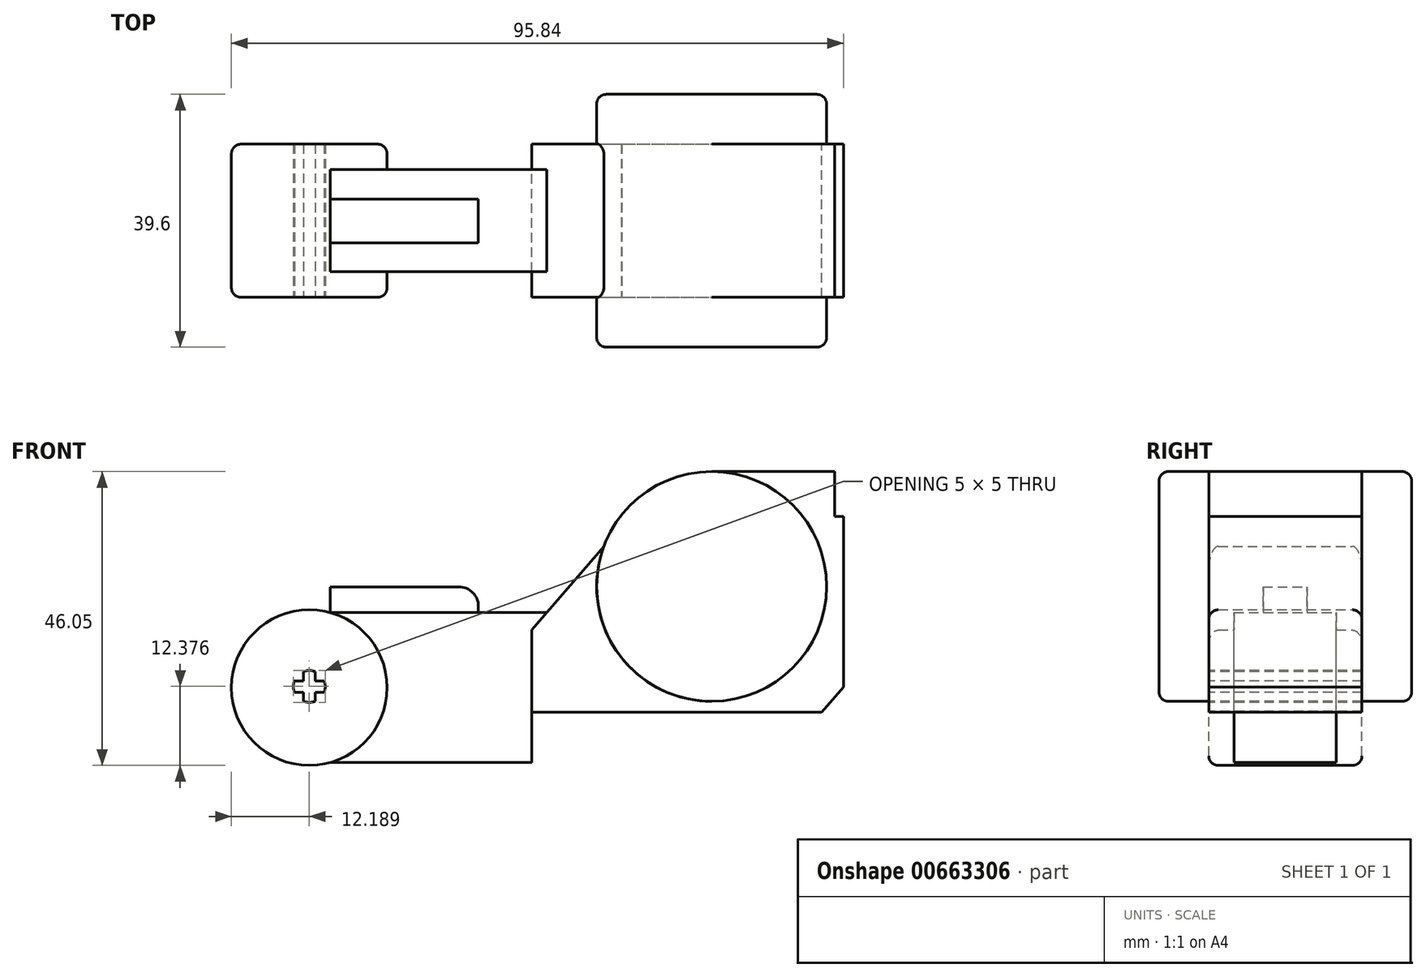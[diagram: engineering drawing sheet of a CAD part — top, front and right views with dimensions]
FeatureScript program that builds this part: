
annotation { "Feature Type Name" : "Feature", "Feature Type Description" : "" }
export const myFeature = defineFeature(function(context is Context, id is Id, definition is map)
    precondition{}
    {
        {
            var Q0;
            Q0=qCreatedBy(makeId("Front.planeOp"),FACE);
            var sketch = newSketch(context, id + "F0", { "sketchPlane" : qUnion([Q0])});
            skLineSegment(sketch, "E0.bottom", {"start": v(16.93, 23.2) * mm, "end": v(-2.37, 23.2) * mm});
            skLineSegment(sketch, "E0.top", {"start": v(7.98, -22.4) * mm, "end": v(-62.12, -22.4) * mm});
            skLineSegment(sketch, "E0.left", {"start": v(30.68, 16.16) * mm, "end": v(30.68, -6.44) * mm});
            skPoint(sketch, "E0.middle", {"position": v(-23.2, 0.4) * mm});
            skLineSegment(sketch, "E1.bottom", {"start": v(-62.12, -22.4) * mm, "end": v(7.98, -22.4) * mm});
            skLineSegment(sketch, "E2.bottom", {"start": v(-62.12, -22.4) * mm, "end": v(-30.52, -22.4) * mm});
            skPoint(sketch, "E3.endSnap0", {"position": v(30.68, 0.4) * mm});
            skLineSegment(sketch, "E4.right", {"start": v(30.68, -14.8) * mm, "end": v(30.68, -14.5) * mm});
            skPoint(sketch, "E5.oppositeSnap0", {"position": v(24.48, 14.62) * mm});
            skLineSegment(sketch, "E5.bottom", {"start": v(7.98, -22.4) * mm, "end": v(-30.52, -22.4) * mm});
            skLineSegment(sketch, "E6.bottom", {"start": v(-30.52, -22.4) * mm, "end": v(7.98, -22.4) * mm});
            skLineSegment(sketch, "E6.top", {"start": v(-30.52, -4.4) * mm, "end": v(-17.6, -4.4) * mm});
            skLineSegment(sketch, "E6.left", {"start": v(-30.52, -22.4) * mm, "end": v(-30.52, -4.4) * mm});
            skLineSegment(sketch, "E7.bottom", {"start": v(-2.37, 23.2) * mm, "end": v(16.93, 23.2) * mm});
            skLineSegment(sketch, "E7.top", {"start": v(-31.78, -14.5) * mm, "end": v(14.85, -14.5) * mm});
            skLineSegment(sketch, "E8", {"start": v(68.58, 23.2) * mm, "end": v(68.58, 5.2) * mm, "construction": true});
            skPoint(sketch, "E9.endSnap0", {"position": v(68.58, 5.2) * mm});
            skLineSegment(sketch, "E10", {"start": v(-2.37, 5.2) * mm, "end": v(-2.37, 31.5) * mm, "construction": true});
            skPoint(sketch, "E10.startSnap0", {"position": v(-2.37, 31.5) * mm});
            skCircle(sketch, "E11", {"center": v(-2.37, 5.2) * mm, "radius": 18 * mm});
            skPoint(sketch, "E12.end.orphan", {"position": v(15.63, 38.6) * mm});
            skPoint(sketch, "E12.start.orphan", {"position": v(-77.07, 38.6) * mm});
            skPoint(sketch, "E13.orphan", {"position": v(68.58, -12.8) * mm});
            skLineSegment(sketch, "E14.trimOffspring", {"start": v(18.28, 5.2) * mm, "end": v(-2.37, 5.2) * mm, "construction": true});
            skPoint(sketch, "E9.start.orphan", {"position": v(68.58, 5.2) * mm});
            skLineSegment(sketch, "E15.bottom", {"start": v(-62.12, -22.4) * mm, "end": v(-14.02, -22.4) * mm});
            skLineSegment(sketch, "E15.top", {"start": v(-62.12, 1.1) * mm, "end": v(-28.16, 1.1) * mm});
            skLineSegment(sketch, "E16", {"start": v(30.68, 0.4) * mm, "end": v(18.28, 0.55) * mm, "construction": true});
            skLineSegment(sketch, "E17", {"start": v(-28.16, 1.1) * mm, "end": v(-19.23, 11.5) * mm});
            skPoint(sketch, "E18.orphan", {"position": v(-77.07, 23.2) * mm});
            skPoint(sketch, "E19.orphan", {"position": v(-30.52, 23.2) * mm});
            skLineSegment(sketch, "E20", {"start": v(41.56, -22.4) * mm, "end": v(41.56, 16.16) * mm, "construction": true});
            skLineSegment(sketch, "E21", {"start": v(18.28, 16.16) * mm, "end": v(30.68, 16.16) * mm});
            skLineSegment(sketch, "E22", {"start": v(18.28, 16.16) * mm, "end": v(18.28, -6.3) * mm});
            skLineSegment(sketch, "E23", {"start": v(18.28, -6.3) * mm, "end": v(30.68, -6.44) * mm});
            skLineSegment(sketch, "E24", {"start": v(18.28, -6.3) * mm, "end": v(18.28, -10.54) * mm});
            skPoint(sketch, "E3.end.orphan", {"position": v(30.68, -14.8) * mm});
            skLineSegment(sketch, "E25", {"start": v(18.28, -10.54) * mm, "end": v(7.98, -22.4) * mm});
            skLineSegment(sketch, "E26", {"start": v(-77.07, 13.22) * mm, "end": v(-53.67, 13.22) * mm, "construction": true});
            skCircle(sketch, "E27", {"center": v(-65.37, -10.64) * mm, "radius": 12.2 * mm});
            skPoint(sketch, "E27.centerSnap0", {"position": v(-65.37, 13.22) * mm});
            skPoint(sketch, "E27.centerSnap1", {"position": v(-77.07, -10.64) * mm});
            skPoint(sketch, "E0.right.start.orphan", {"position": v(-77.07, 1.1) * mm});
            skPoint(sketch, "E28.orphan", {"position": v(-77.07, -22.4) * mm});
            skLineSegment(sketch, "E29", {"start": v(-28.16, 1.1) * mm, "end": v(-30.52, -1.63) * mm});
            skLineSegment(sketch, "E30", {"start": v(-30.52, -1.63) * mm, "end": v(-30.52, -4.4) * mm});
            skLineSegment(sketch, "E31.top", {"start": v(30.68, 16.16) * mm, "end": v(16.93, 16.16) * mm});
            skLineSegment(sketch, "E31.right", {"start": v(16.93, 23.2) * mm, "end": v(16.93, 16.16) * mm});
            skPoint(sketch, "E32.orphan", {"position": v(30.68, 23.2) * mm});
            skLineSegment(sketch, "E33.trimOffspring", {"start": v(30.68, -6.44) * mm, "end": v(30.68, -4.4) * mm});
            skLineSegment(sketch, "E34.trimOffspring", {"start": v(30.68, -6.44) * mm, "end": v(30.68, 14.62) * mm});
            skLineSegment(sketch, "E35.trimOffspring", {"start": v(30.68, -14.5) * mm, "end": v(30.68, -14.8) * mm});
            skPoint(sketch, "E36.orphan", {"position": v(30.68, -22.4) * mm});
            skLineSegment(sketch, "E37", {"start": v(18.28, -10.54) * mm, "end": v(18.28, -14.5) * mm});
            skPoint(sketch, "E38.trimOffspring.end.orphan", {"position": v(18.28, -14.8) * mm});
            skLineSegment(sketch, "E39", {"start": v(18.28, -14.5) * mm, "end": v(14.85, -14.5) * mm});
            skLineSegment(sketch, "E40", {"start": v(-30.52, -22.4) * mm, "end": v(-30.52, -14.5) * mm});
            skLineSegment(sketch, "E41", {"start": v(-30.52, -14.5) * mm, "end": v(-16.42, -14.5) * mm});
            skLineSegment(sketch, "E42", {"start": v(-30.52, -22.4) * mm, "end": v(-23.37, -22.4) * mm});
            skSolve(sketch);
        }
        {
            var Q0;
            {var subQ0=sQuery(id+"F0.wireOp",EDGE,"E11");var subQ1=makeQuery(id+"F0.imprint","INTERSECT",VERTEX,{"derivedFrom":[sQuery(id+"F0.wireOp",EDGE,"E7.bottom"),subQ0]});Q0=makeQuery(id+"F0.imprint","IMPRINT",FACE,{"disambiguationData":[TD([[makeQuery(id+"F0.imprint","IMPRINT",EDGE,{"disambiguationData":[TD([[subQ1,-1.0]])],"derivedFrom":subQ0}),1.0]])]});}
            extrude(context, id + "F1", {"entities" : qUnion([Q0]), "endBound" : BoundingType.SYMMETRIC, "oppositeDirection" : true, "depth" : 39.6 * mm, "offsetDistance" : 25 * mm});
        }
        {
            var Q0;
            {var subQ1=sQuery(id+"F0.wireOp",EDGE,"E6.bottom");Q0=makeQuery(id+"F0.imprint","IMPRINT",FACE,{"disambiguationData":[TD([[makeQuery(id+"F0.imprint","IMPRINT",EDGE,{"derivedFrom":subQ1}),1.0]])]});}
            var Q1;
            {var subQ4=sQuery(id+"F0.wireOp",EDGE,"E6.top");Q1=makeQuery(id+"F0.imprint","IMPRINT",FACE,{"disambiguationData":[TD([[makeQuery(id+"F0.imprint","IMPRINT",EDGE,{"derivedFrom":subQ4}),-1.0]])]});}
            var Q2;
            {var subQ2=sQuery(id+"F0.wireOp",EDGE,"E6.top");Q2=makeQuery(id+"F0.imprint","IMPRINT",FACE,{"disambiguationData":[TD([[makeQuery(id+"F0.imprint","IMPRINT",EDGE,{"derivedFrom":subQ2}),1.0]])]});}
            var Q3;
            {var subQ1=sQuery(id+"F0.wireOp",EDGE,"E0.left");Q3=makeQuery(id+"F0.imprint","IMPRINT",FACE,{"disambiguationData":[TD([[makeQuery(id+"F0.imprint","IMPRINT",EDGE,{"derivedFrom":subQ1}),-1.0]])]});}
            extrude(context, id + "F2", {"entities" : qUnion([Q0, Q1, Q2, Q3]), "operationType" : NewBodyOperationType.ADD, "endBound" : BoundingType.SYMMETRIC, "depth" : 24 * mm, "offsetDistance" : 25 * mm});
        }
        {
            var Q0;
            {var subQ7=sQuery(id+"F0.wireOp",EDGE,"E15.top");Q0=makeQuery(id+"F0.imprint","IMPRINT",FACE,{"disambiguationData":[TD([[makeQuery(id+"F0.imprint","IMPRINT",EDGE,{"derivedFrom":subQ7}),-1.0]])]});}
            extrude(context, id + "F3", {"entities" : qUnion([Q0]), "operationType" : NewBodyOperationType.ADD, "endBound" : BoundingType.SYMMETRIC, "depth" : 16 * mm, "offsetDistance" : 25 * mm});
        }
        {
            var Q0;
            {var subQ0=sQuery(id+"F0.wireOp",EDGE,"E27");var subQ1=makeQuery(id+"F0.imprint","INTERSECT",VERTEX,{"derivedFrom":[sQuery(id+"F0.wireOp",EDGE,"E15.bottom"),subQ0]});Q0=makeQuery(id+"F0.imprint","IMPRINT",FACE,{"disambiguationData":[TD([[makeQuery(id+"F0.imprint","IMPRINT",EDGE,{"disambiguationData":[TD([[subQ1,1.0]])],"derivedFrom":subQ0}),1.0]])]});}
            extrude(context, id + "F4", {"entities" : qUnion([Q0]), "operationType" : NewBodyOperationType.ADD, "endBound" : BoundingType.SYMMETRIC, "depth" : 24 * mm, "offsetDistance" : 25 * mm});
        }
        {
            var Q0;
            Q0=makeQuery(id+"F4.opExtrude","CAP_FACE",FACE,{"disambiguationData":[OSD([sQuery(id+"F0.wireOp",EDGE,"E27")])],"isStart":false});
            var sketch = newSketch(context, id + "F5", { "sketchPlane" : qUnion([Q0])});
            skCircle(sketch, "E43", {"center": v(-65.37, -10.46) * mm, "radius": 3.5 * mm});
            skCircle(sketch, "E44", {"center": v(-65.37, -10.46) * mm, "radius": 2.5 * mm});
            skLineSegment(sketch, "E45", {"start": v(-65.37, -10.46) * mm, "end": v(-66.27, -10.46) * mm});
            skLineSegment(sketch, "E46", {"start": v(-66.27, -10.46) * mm, "end": v(-64.47, -10.46) * mm});
            skLineSegment(sketch, "E47", {"start": v(-65.37, -10.46) * mm, "end": v(-65.37, -11.36) * mm});
            skLineSegment(sketch, "E48", {"start": v(-65.37, -11.36) * mm, "end": v(-65.37, -9.56) * mm});
            skLineSegment(sketch, "E49", {"start": v(-66.27, -9.6) * mm, "end": v(-67.72, -9.6) * mm});
            skLineSegment(sketch, "E50", {"start": v(-66.27, -9.6) * mm, "end": v(-66.27, -8.13) * mm});
            skLineSegment(sketch, "E51", {"start": v(-64.47, -9.6) * mm, "end": v(-64.47, -8.13) * mm});
            skLineSegment(sketch, "E52", {"start": v(-64.47, -9.6) * mm, "end": v(-63.02, -9.6) * mm});
            skLineSegment(sketch, "E53", {"start": v(-66.27, -11.36) * mm, "end": v(-67.7, -11.36) * mm});
            skLineSegment(sketch, "E54", {"start": v(-66.27, -11.36) * mm, "end": v(-66.27, -12.8) * mm});
            skLineSegment(sketch, "E55", {"start": v(-64.47, -11.36) * mm, "end": v(-64.47, -12.8) * mm});
            skLineSegment(sketch, "E56", {"start": v(-64.47, -11.36) * mm, "end": v(-63.04, -11.36) * mm});
            skSolve(sketch);
        }
        {
            var Q0;
            {var subQ4=sQuery(id+"F5.wireOp",EDGE,"E49");Q0=makeQuery(id+"F5.imprint","IMPRINT",FACE,{"disambiguationData":[TD([[makeQuery(id+"F5.imprint","IMPRINT",EDGE,{"derivedFrom":subQ4}),1.0]])]});}
            extrude(context, id + "F6", {"entities" : qUnion([Q0]), "operationType" : NewBodyOperationType.REMOVE, "oppositeDirection" : true, "depth" : 25 * mm, "offsetDistance" : 25 * mm});
        }
        {
            var Q0;
            Q0=makeQuery(id+"F4.opExtrude","CAP_EDGE",EDGE,{"disambiguationData":[OSD([sQuery(id+"F0.wireOp",EDGE,"E27")])],"isStart":true});
            fillet(context, id + "F7", {"entities" : qUnion([Q0]), "radius" : 1.5 * mm, "tangentPropagation" : true, "allowEdgeOverflow" : false});
        }
        {
            var Q0;
            Q0=makeQuery(id+"F4.opExtrude","CAP_EDGE",EDGE,{"disambiguationData":[OSD([sQuery(id+"F0.wireOp",EDGE,"E27")])],"isStart":false});
            fillet(context, id + "F8", {"entities" : qUnion([Q0]), "radius" : 1.5 * mm, "tangentPropagation" : true, "allowEdgeOverflow" : false});
        }
        {
            var Q0;
            Q0=makeQuery(id+"F2.opExtrude","CAP_EDGE",EDGE,{"disambiguationData":[OSD([sQuery(id+"F0.wireOp",EDGE,"E17"),sQuery(id+"F0.wireOp",EDGE,"E29")])],"isStart":false});
            fillet(context, id + "F9", {"entities" : qUnion([Q0]), "radius" : 1.5 * mm, "tangentPropagation" : true, "allowEdgeOverflow" : false});
        }
        {
            var Q0;
            Q0=makeQuery(id+"F2.opExtrude","CAP_EDGE",EDGE,{"disambiguationData":[OSD([sQuery(id+"F0.wireOp",EDGE,"E17"),sQuery(id+"F0.wireOp",EDGE,"E29")])],"isStart":true});
            fillet(context, id + "F10", {"entities" : qUnion([Q0]), "radius" : 1.5 * mm, "tangentPropagation" : true, "allowEdgeOverflow" : false});
        }
        {
            var Q0;
            Q0=makeQuery(id+"F1.opExtrude","CAP_EDGE",EDGE,{"disambiguationData":[OSD([sQuery(id+"F0.wireOp",EDGE,"E11")])],"isStart":false});
            fillet(context, id + "F11", {"entities" : qUnion([Q0]), "radius" : 1.5 * mm, "tangentPropagation" : true, "allowEdgeOverflow" : false});
        }
        {
            var Q0;
            Q0=makeQuery(id+"F1.opExtrude","CAP_EDGE",EDGE,{"disambiguationData":[OSD([sQuery(id+"F0.wireOp",EDGE,"E11")])],"isStart":true});
            fillet(context, id + "F12", {"entities" : qUnion([Q0]), "radius" : 1.5 * mm, "tangentPropagation" : true, "allowEdgeOverflow" : false});
        }
        {
            var Q0;
            Q0=makeQuery(id+"F2.opExtrude","CAP_FACE",FACE,{"disambiguationData":[OSD([sQuery(id+"F0.wireOp",EDGE,"E6.bottom"),sQuery(id+"F0.wireOp",EDGE,"E6.left"),sQuery(id+"F0.wireOp",EDGE,"E7.bottom"),sQuery(id+"F0.wireOp",EDGE,"E0.left"),sQuery(id+"F0.wireOp",EDGE,"E11"),sQuery(id+"F0.wireOp",EDGE,"E15.bottom"),sQuery(id+"F0.wireOp",EDGE,"E17"),sQuery(id+"F0.wireOp",EDGE,"E23"),sQuery(id+"F0.wireOp",EDGE,"E24"),sQuery(id+"F0.wireOp",EDGE,"E25"),sQuery(id+"F0.wireOp",EDGE,"E29"),sQuery(id+"F0.wireOp",EDGE,"E30"),sQuery(id+"F0.wireOp",EDGE,"E31.top"),sQuery(id+"F0.wireOp",EDGE,"E31.right"),sQuery(id+"F0.wireOp",EDGE,"E34.trimOffspring"),sQuery(id+"F0.wireOp",EDGE,"E40"),sQuery(id+"F0.wireOp",EDGE,"E42")])],"isStart":false});
            var sketch = newSketch(context, id + "F13", { "sketchPlane" : qUnion([Q0])});
            skLineSegment(sketch, "E57", {"start": v(-30.52, -22.4) * mm, "end": v(-30.52, -14.4) * mm});
            skLineSegment(sketch, "E58", {"start": v(-30.52, -14.4) * mm, "end": v(-16.42, -14.4) * mm});
            skLineSegment(sketch, "E59", {"start": v(-16.42, -14.4) * mm, "end": v(-16.42, -22.4) * mm});
            skLineSegment(sketch, "E60", {"start": v(-30.52, -22.4) * mm, "end": v(-23.37, -22.4) * mm});
            skLineSegment(sketch, "E61", {"start": v(-23.37, -22.4) * mm, "end": v(-16.42, -14.4) * mm});
            skLineSegment(sketch, "E62", {"start": v(-16.42, -14.4) * mm, "end": v(14.94, -14.4) * mm});
            skLineSegment(sketch, "E63", {"start": v(-16.42, -22.4) * mm, "end": v(-16.42, -18.4) * mm});
            skCircle(sketch, "E64", {"center": v(-9.36, -18.4) * mm, "radius": 2.5 * mm});
            skCircle(sketch, "E65", {"center": v(-9.36, -18.4) * mm, "radius": 3 * mm});
            skCircle(sketch, "E66", {"center": v(-1.36, -18.4) * mm, "radius": 2.5 * mm});
            skCircle(sketch, "E67", {"center": v(-1.36, -18.4) * mm, "radius": 3 * mm});
            skCircle(sketch, "E68", {"center": v(6.64, -18.4) * mm, "radius": 2.5 * mm});
            skCircle(sketch, "E69", {"center": v(6.64, -18.4) * mm, "radius": 3 * mm});
            skLineSegment(sketch, "E70", {"start": v(18.28, -10.54) * mm, "end": v(18.28, -14.4) * mm});
            skLineSegment(sketch, "E71", {"start": v(14.94, -14.4) * mm, "end": v(18.28, -14.4) * mm});
            skSolve(sketch);
        }
        {
            var Q0;
            Q0=makeQuery(id+"F13.imprint","IMPRINT",FACE,{"disambiguationData":[TD([[makeQuery(id+"F13.imprint","IMPRINT",EDGE,{"derivedFrom":sQuery(id+"F13.wireOp",EDGE,"E64")}),1.0]])]});
            var Q1;
            Q1=makeQuery(id+"F13.imprint","IMPRINT",FACE,{"disambiguationData":[TD([[makeQuery(id+"F13.imprint","IMPRINT",EDGE,{"derivedFrom":sQuery(id+"F13.wireOp",EDGE,"E66")}),1.0]])]});
            var Q2;
            Q2=makeQuery(id+"F13.imprint","IMPRINT",FACE,{"disambiguationData":[TD([[makeQuery(id+"F13.imprint","IMPRINT",EDGE,{"derivedFrom":sQuery(id+"F13.wireOp",EDGE,"E68")}),1.0]])]});
            var Q3;
            Q3=makeQuery(id+"F13.imprint","IMPRINT",FACE,{"disambiguationData":[TD([[makeQuery(id+"F13.imprint","IMPRINT",EDGE,{"derivedFrom":sQuery(id+"F13.wireOp",EDGE,"E59")}),-1.0]])]});
            extrude(context, id + "F14", {"entities" : qUnion([Q0, Q1, Q2, Q3]), "operationType" : NewBodyOperationType.REMOVE, "oppositeDirection" : true, "depth" : 25 * mm, "offsetDistance" : 25 * mm});
        }
        {
            var Q0;
            Q0=makeQuery(id+"F3.opExtrude","SWEPT_FACE",FACE,{"disambiguationData":[OSD([sQuery(id+"F0.wireOp",EDGE,"E15.top")])]});
            var sketch = newSketch(context, id + "F15", { "sketchPlane" : qUnion([Q0])});
            skLineSegment(sketch, "E72", {"start": v(-38.88, 0) * mm, "end": v(-38.88, 3.41) * mm});
            skLineSegment(sketch, "E73", {"start": v(-38.88, 3.41) * mm, "end": v(-38.88, -3.49) * mm});
            skLineSegment(sketch, "E74", {"start": v(-38.88, -3.49) * mm, "end": v(-66.47, -3.49) * mm});
            skLineSegment(sketch, "E75", {"start": v(-38.88, 3.41) * mm, "end": v(-66.47, 3.41) * mm});
            skLineSegment(sketch, "E76", {"start": v(-66.47, 3.41) * mm, "end": v(-66.47, -3.49) * mm});
            skSolve(sketch);
        }
        {
            var Q0;
            {var subQ1=sQuery(id+"F15.wireOp",EDGE,"E73");var subQ8=makeQuery(id+"F15.imprint","IMPRINT",VERTEX,{"derivedFrom":subQ1});Q0=makeQuery(id+"F15.imprint","IMPRINT",FACE,{"disambiguationData":[TD([[makeQuery(id+"F15.imprint","IMPRINT",EDGE,{"disambiguationData":[TD([[subQ8,1.0]])],"derivedFrom":subQ1}),-1.0]])]});}
            extrude(context, id + "F16", {"entities" : qUnion([Q0]), "operationType" : NewBodyOperationType.ADD, "endBound" : BoundingType.SYMMETRIC, "depth" : 8.08 * mm, "offsetDistance" : 25 * mm});
        }
        {
            var Q0;
            Q0=makeQuery(id+"F16.opExtrude","CAP_EDGE",EDGE,{"disambiguationData":[OSD([sQuery(id+"F15.wireOp",EDGE,"E73")])],"isStart":false});
            fillet(context, id + "F17", {"entities" : qUnion([Q0]), "radius" : 3.05 * mm, "tangentPropagation" : true, "allowEdgeOverflow" : false});
        }
    });
